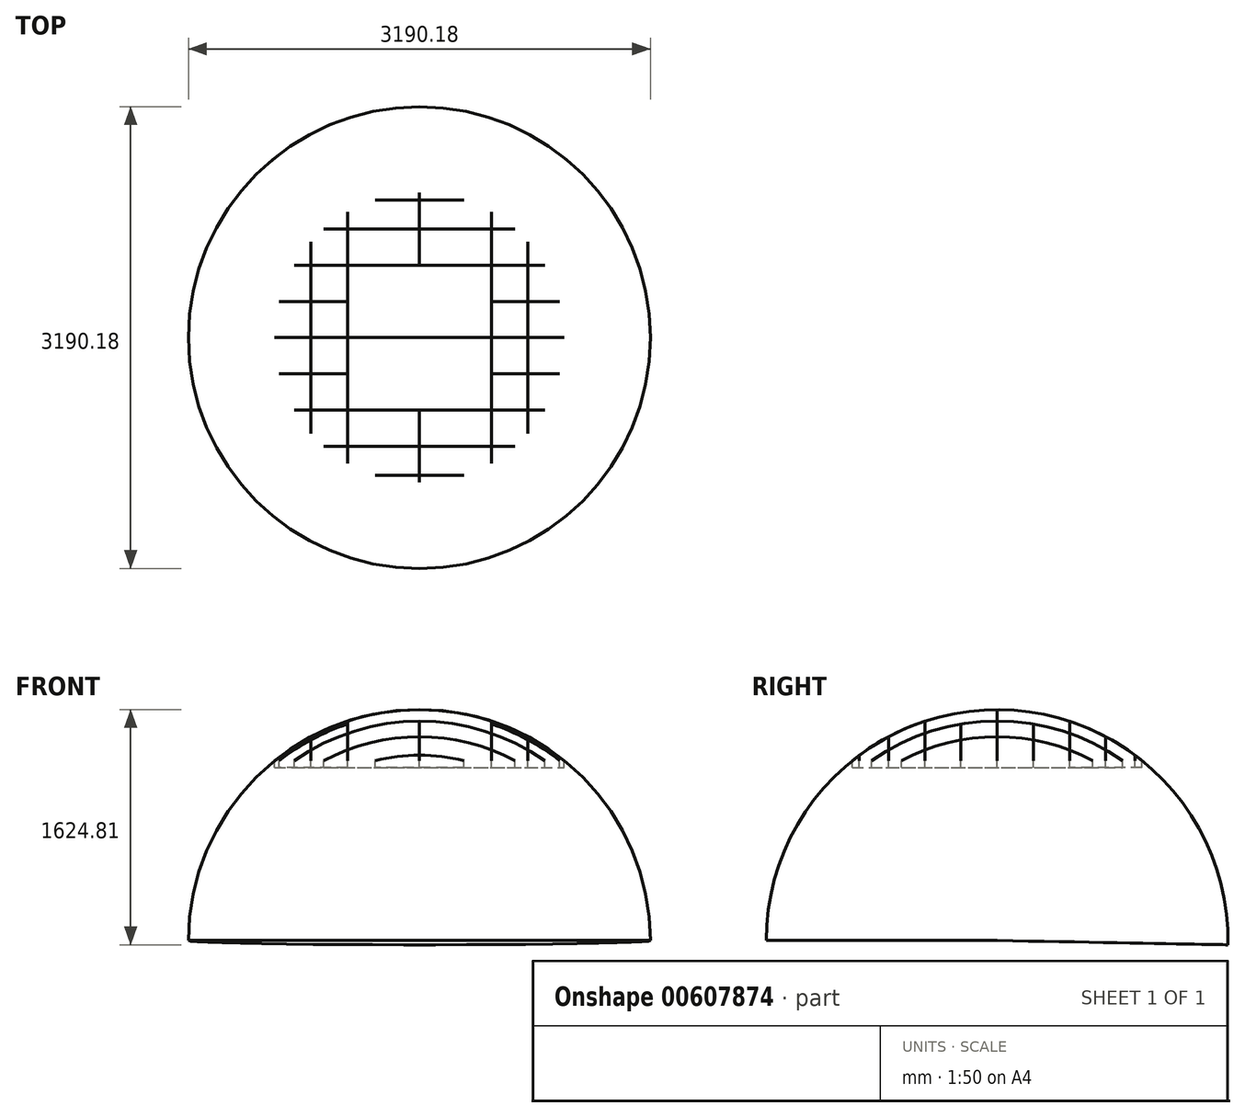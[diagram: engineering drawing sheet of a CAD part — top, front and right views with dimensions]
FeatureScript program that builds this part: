
annotation { "Feature Type Name" : "Feature", "Feature Type Description" : "" }
export const myFeature = defineFeature(function(context is Context, id is Id, definition is map)
    precondition{}
    {
        {
            var Q0;
            Q0=qCreatedBy(makeId("Top.planeOp"),FACE);
            var sketch = newSketch(context, id + "F0", { "sketchPlane" : qUnion([Q0])});
            skLineSegment(sketch, "E0", {"start": v(-1000, 0) * mm, "end": v(1000, 0) * mm});
            skCircle(sketch, "E1", {"center": v(0, 0) * mm, "radius": 1000 * mm});
            skPoint(sketch, "E2", {"position": v(500, 0) * mm});
            skPoint(sketch, "E3", {"position": v(-500, 0) * mm});
            skPoint(sketch, "E4", {"position": v(750, 0) * mm});
            skPoint(sketch, "E5", {"position": v(-750, 0) * mm});
            skLineSegment(sketch, "E6", {"start": v(-749.8, -661.67) * mm, "end": v(-749.8, 661.67) * mm});
            skLineSegment(sketch, "E7", {"start": v(-496.8, -867.86) * mm, "end": v(-496.8, 867.86) * mm});
            skLineSegment(sketch, "E8", {"start": v(0, -1000) * mm, "end": v(0, 1000) * mm, "construction": true});
            skPoint(sketch, "E9", {"position": v(0, 500) * mm});
            skPoint(sketch, "E10", {"position": v(0, 750) * mm});
            skPoint(sketch, "E11", {"position": v(-496.8, 250) * mm});
            skLineSegment(sketch, "E12", {"start": v(-496.8, 250) * mm, "end": v(-968.25, 250) * mm});
            skLineSegment(sketch, "E13", {"start": v(-866.14, 499.8) * mm, "end": v(866.14, 499.8) * mm});
            skLineSegment(sketch, "E14", {"start": v(-660.73, 750.63) * mm, "end": v(660.73, 750.63) * mm});
            skLineSegment(sketch, "E15", {"start": v(0, 1000) * mm, "end": v(0, 500) * mm});
            skLineSegment(sketch, "E16.MirrorCS", {"start": v(496.8, -867.86) * mm, "end": v(496.8, 867.86) * mm});
            skLineSegment(sketch, "E17.MirrorCS", {"start": v(749.8, -661.67) * mm, "end": v(749.8, 661.67) * mm});
            skLineSegment(sketch, "E18.MirrorCS", {"start": v(496.8, 250) * mm, "end": v(968.25, 250) * mm});
            skLineSegment(sketch, "E19.MirrorCS", {"start": v(496.8, -250) * mm, "end": v(968.25, -250) * mm});
            skLineSegment(sketch, "E20.MirrorCS", {"start": v(-866.14, -499.8) * mm, "end": v(866.14, -499.8) * mm});
            skLineSegment(sketch, "E21.MirrorCS", {"start": v(-660.73, -750.63) * mm, "end": v(660.73, -750.63) * mm});
            skLineSegment(sketch, "E22.MirrorCS", {"start": v(-496.8, -250) * mm, "end": v(-968.25, -250) * mm});
            skLineSegment(sketch, "E23.MirrorCS", {"start": v(0, 1000) * mm, "end": v(0, -1000) * mm, "construction": true});
            skPoint(sketch, "E24.MirrorP", {"position": v(0, -500) * mm});
            skLineSegment(sketch, "E25", {"start": v(0, -1000) * mm, "end": v(0, -500) * mm});
            skPoint(sketch, "E26", {"position": v(0, 950) * mm});
            skLineSegment(sketch, "E27", {"start": v(306.37, 951.91) * mm, "end": v(-306.37, 951.91) * mm});
            skLineSegment(sketch, "E28.MirrorCS", {"start": v(306.37, -951.91) * mm, "end": v(-306.37, -951.91) * mm});
            skSolve(sketch);
        }
        {
            var Q0;
            Q0=qCreatedBy(makeId("Top.planeOp"),FACE);
            cPlane(context, id + "F1", {"entities" : qUnion([Q0]), "cplaneType" : CPlaneType.OFFSET, "offset" : 1193.8 * mm, "oppositeDirection" : true, "width" : 152.4 * mm, "height" : 152.4 * mm});
        }
        {
            var Q0;
            Q0=qCreatedBy(id+"F1.planeOp",FACE);
            var sketch = newSketch(context, id + "F2", { "sketchPlane" : qUnion([Q0])});
            skLineSegment(sketch, "E29", {"start": v(-1601.25, 0) * mm, "end": v(1595.09, 0) * mm});
            skArc(sketch, "E30", {"start": v(1595.09, 0) * mm, "mid": v(0, -1595.09) * mm, "end": v(-1595.09, 0) * mm});
            skSolve(sketch);
        }
        {
            var Q0;
            Q0 = qSketchRegion(id + "F2", true);
            var Q1;
            Q1=sQuery(id+"F2.wireOp",EDGE,"E30");
            var Q2;
            Q2=sQuery(id+"F2.wireOp",EDGE,"E29");
            revolve(context, id + "F3", {"bodyType" : ToolBodyType.SURFACE, "entities" : qUnion([Q0]), "surfaceEntities" : qUnion([Q1]), "axis" : qUnion([Q2]), "revolveType" : RevolveType.ONE_DIRECTION, "oppositeDirection" : true, "angle" : 181.07 * degree});
        }
        {
            var Q0;
            Q0=sQuery(id+"F0.wireOp",EDGE,"E6");
            var Q1;
            Q1=sQuery(id+"F0.wireOp",EDGE,"E7");
            var Q2;
            Q2=sQuery(id+"F0.wireOp",EDGE,"E16.MirrorCS");
            var Q3;
            Q3=sQuery(id+"F0.wireOp",EDGE,"E25");
            var Q4;
            Q4=sQuery(id+"F0.wireOp",EDGE,"E17.MirrorCS");
            var Q5;
            Q5=sQuery(id+"F0.wireOp",EDGE,"E15");
            extrude(context, id + "F4", {"bodyType" : ToolBodyType.SURFACE, "surfaceEntities" : qUnion([Q0, Q1, Q2, Q3, Q4, Q5]), "endBound" : BoundingType.UP_TO_NEXT, "depth" : 25.4 * mm, "offsetDistance" : 25.4 * mm});
        }
        {
            var Q0;
            Q0=sQuery(id+"F0.wireOp",EDGE,"E28.MirrorCS");
            var Q1;
            Q1=sQuery(id+"F0.wireOp",EDGE,"E21.MirrorCS");
            var Q2;
            Q2=sQuery(id+"F0.wireOp",EDGE,"E20.MirrorCS");
            var Q3;
            Q3=sQuery(id+"F0.wireOp",EDGE,"E0");
            var Q4;
            Q4=sQuery(id+"F0.wireOp",EDGE,"E13");
            var Q5;
            Q5=sQuery(id+"F0.wireOp",EDGE,"E14");
            var Q6;
            Q6=sQuery(id+"F0.wireOp",EDGE,"E27");
            var Q7;
            Q7=sQuery(id+"F0.wireOp",EDGE,"E18.MirrorCS");
            var Q8;
            Q8=sQuery(id+"F0.wireOp",EDGE,"E19.MirrorCS");
            var Q9;
            Q9=sQuery(id+"F0.wireOp",EDGE,"E12");
            var Q10;
            Q10=sQuery(id+"F0.wireOp",EDGE,"E22.MirrorCS");
            extrude(context, id + "F5", {"bodyType" : ToolBodyType.SURFACE, "surfaceEntities" : qUnion([Q0, Q1, Q2, Q3, Q4, Q5, Q6, Q7, Q8, Q9, Q10]), "endBound" : BoundingType.UP_TO_NEXT, "depth" : 25.4 * mm, "offsetDistance" : 25.4 * mm});
        }
    });
